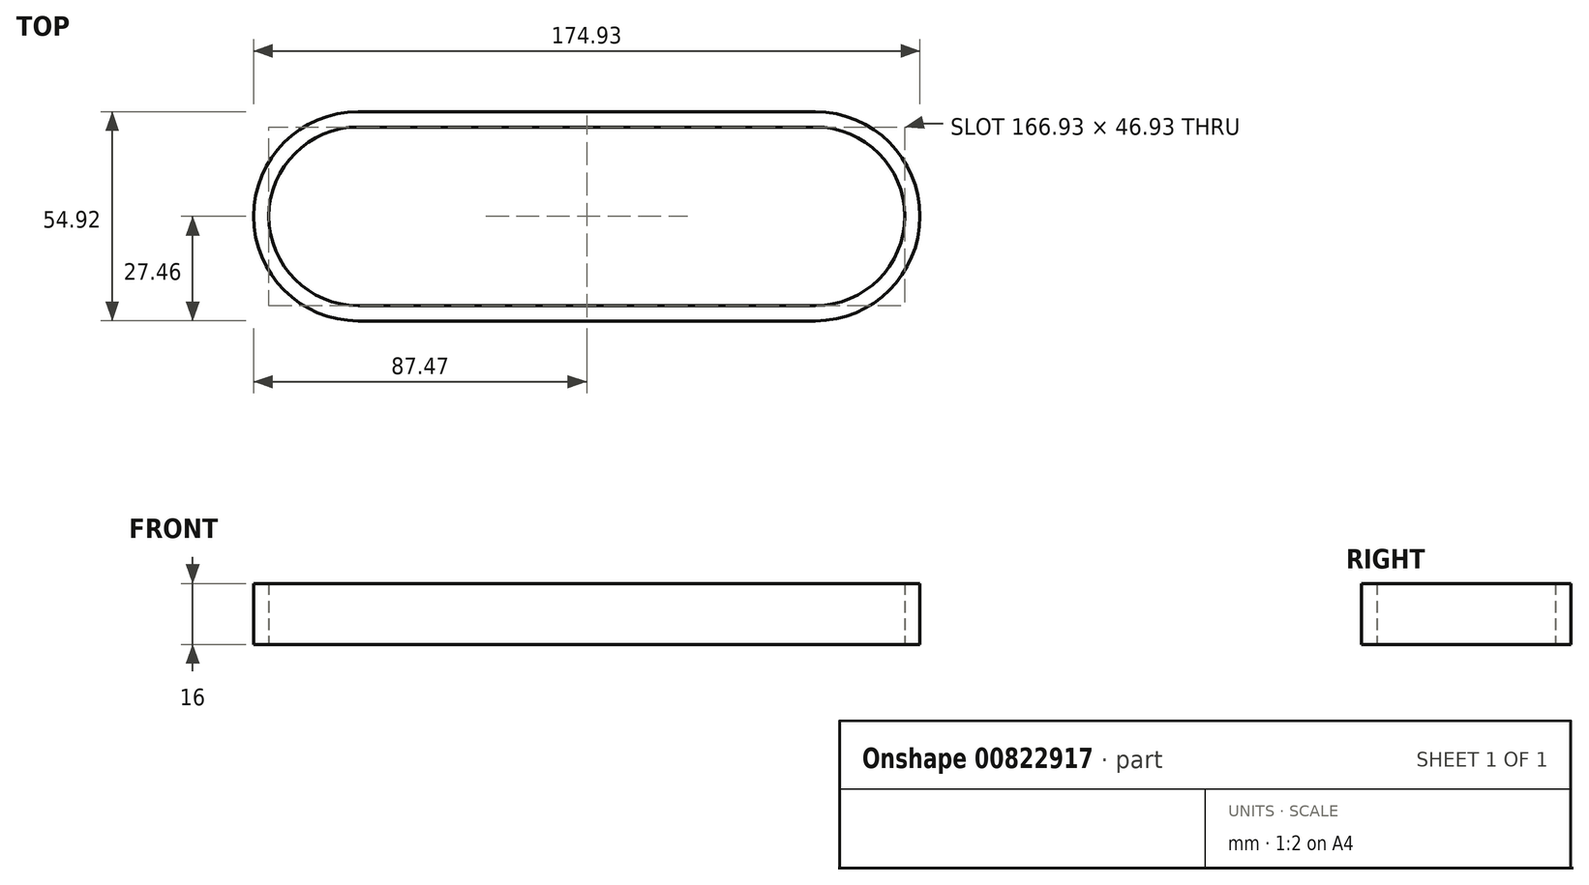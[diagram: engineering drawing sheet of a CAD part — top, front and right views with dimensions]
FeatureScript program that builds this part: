
annotation { "Feature Type Name" : "Feature", "Feature Type Description" : "" }
export const myFeature = defineFeature(function(context is Context, id is Id, definition is map)
    precondition{}
    {
        {
            var Q0;
            Q0=qCreatedBy(makeId("Top.planeOp"),FACE);
            var sketch = newSketch(context, id + "F0", { "sketchPlane" : qUnion([Q0])});
            skArc(sketch, "E0", {"start": v(0, -25.46) * mm, "mid": v(25.46, 0) * mm, "end": v(0, 25.46) * mm, "construction": true});
            skLineSegment(sketch, "E1", {"start": v(0, 0) * mm, "end": v(-120, 0) * mm, "construction": true});
            skArc(sketch, "E2", {"start": v(-120, 25.46) * mm, "mid": v(-145.47, 0) * mm, "end": v(-120, -25.46) * mm, "construction": true});
            skLineSegment(sketch, "E3", {"start": v(0, 0) * mm, "end": v(0, 25.46) * mm, "construction": true});
            skLineSegment(sketch, "E4", {"start": v(0, 0) * mm, "end": v(0, -25.46) * mm, "construction": true});
            skLineSegment(sketch, "E5", {"start": v(-120, 0) * mm, "end": v(-120, 25.46) * mm, "construction": true});
            skLineSegment(sketch, "E6", {"start": v(-120, 0) * mm, "end": v(-120, -25.46) * mm, "construction": true});
            skLineSegment(sketch, "E7", {"start": v(-120, 25.46) * mm, "end": v(0, 25.47) * mm, "construction": true});
            skLineSegment(sketch, "E8", {"start": v(-120, -25.46) * mm, "end": v(0, -25.47) * mm, "construction": true});
            skArc(sketch, "E9.0", {"start": v(-120, 23.46) * mm, "mid": v(-143.47, 0) * mm, "end": v(-120, -23.46) * mm});
            skLineSegment(sketch, "E10.0", {"start": v(-120, 23.47) * mm, "end": v(0, 23.47) * mm});
            skLineSegment(sketch, "E11.0", {"start": v(-120, -27.46) * mm, "end": v(0, -27.47) * mm});
            skArc(sketch, "E12.0", {"start": v(-120, 27.47) * mm, "mid": v(-147.47, 0) * mm, "end": v(-120, -27.47) * mm});
            skLineSegment(sketch, "E13.0", {"start": v(-120, 27.47) * mm, "end": v(0, 27.46) * mm});
            skArc(sketch, "E14.0", {"start": v(0, -27.47) * mm, "mid": v(27.47, 0) * mm, "end": v(0, 27.47) * mm});
            skArc(sketch, "E15.0", {"start": v(0, -23.46) * mm, "mid": v(23.46, 0) * mm, "end": v(0, 23.46) * mm});
            skLineSegment(sketch, "E16.0", {"start": v(-120, -23.47) * mm, "end": v(0, -23.47) * mm});
            skSolve(sketch);
        }
        {
            var Q0;
            Q0 = qSketchRegion(id + "F0", true);
            extrude(context, id + "F1", {"entities" : qUnion([Q0]), "endBound" : BoundingType.SYMMETRIC, "depth" : 16 * mm, "offsetDistance" : 25 * mm});
        }
    });
